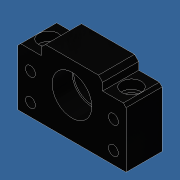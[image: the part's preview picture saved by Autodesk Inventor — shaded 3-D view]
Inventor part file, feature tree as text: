
AUTODESK INVENTOR PART (.ipt)
format: ipt  version: 2013 SP1 (Build 170176100, 176)  size: 166,912 bytes
history: native  units: in
note: dims shown in document units (in); Inventor stores cm internally (conversion verified against a paired STEP export)
features: sketch x4, projected_geometry x4, hole x3, chamfer x2, extrude x1
ambient origin geometry x8: Origin, YZ Plane, XZ Plane, XY Plane, X Axis, Y Axis, Z Axis, Center Point
bodies: Solid1 (feature_tree)
feature tree (14):
  extrude  "Extrusion1"  Depth=1.5354in
  hole  "Hole1"  [1 undecoded]
  hole  "Hole2"  [1 undecoded]
  hole  "Hole3"  [1 undecoded]
  chamfer  "Chamfer1"  Distance=1.811in
  chamfer  "Chamfer2"  Distance=1.811in
  sketch  "Sketch1"  dims[d0=2.3622in d1=1.5354in]
  sketch  "Sketch2"  dims[d2=1.3386in d3=1.2795in]
  projected_geometry  "Projected Loop1"
  sketch  "Sketch3"  dims[d4=0.7874in d5=0.0in d6=0.8661in]
  projected_geometry  "Projected Loop2"
  sketch  "Sketch4"  dims[d7=0.7874in d8=0.75in d9=0.8661in d10=0.4331in d11=0.5635in d12=1.0in d13=0.8108in d14=0.5906in d16=1.811in d17=0.2165in d18=0.75in d19=0.8661in d20=0.2362in d21=0.5635in d22=1.0in d23=0.8108in d24=1.811in d26=0.2598in d27=0.75in d28=0.4252in d29=0.1969in d30=0.5635in d31=1.0in d32=0.8108in d33=0.09in d34=0.125in d35=45.0deg d36=0.06in d37=0.125in d38=45.0deg]
  projected_geometry  "Projected Loop3"
  projected_geometry  "Projected Loop4"
note: 3 required parameter values undecoded (feature->parameter linkage not recoverable at this tier; creation-order binding heuristic only, values carry confidence <= 0.55)
